# Revit family: RE-SERIES
name_source: partatom
category: Generic Models
revit_build: Autodesk Revit LT 2016 (Build: 20161004_0715(x64)
units: mm (PartAtom-declared; Revit-internal decimal feet)

## family parameters
Always vertical = Yes
Can host rebar = No
Cut with Voids When Loaded = No
Part Type = Normal
Room Calculation Point = No
Round Connector Dimension = Use Diameter
Shared = No
Work Plane-Based = No

## types (6) — shared parameters
Manufacturer = REVERSOMATIC
Submittals = http://www.reversomatic.com
URL = http://www.reversomatic.com

## per-type parameters (varying)
| type | A | B | BB | BBB | C | CC | D | DD | G | J | O | U | U2 |
| RE12 | 32.38 " | 24.62 " | 6.16 " | -6.16 " | 13.12 " | 6.56 " | 32 " | 27 " | 23.87 " | 6.5 " | 4.92 " | 154.54° | 52.39° |
| RE7 | 20.38 " | 16.62 " | 4.16 " | -4.16 " | 9 " | 4.5 " | 20 " | 15 " | 15.87 " | 2.5 " | 3.32 " | 140.00° | 60.00° |
| RE9 | 24.38 " | 19.38 " | 4.85 " | -4.85 " | 10.62 " | 5.31 " | 24 " | 19 " | 18.63 " | 9.47 " | 3.88 " | 146.74° | 60.19° |
| RE15 | 36.38 " | 28.38 " | 7.1 " | -7.1 " | 14.88 " | 7.44 " | 36 " | 31 " | 27.63 " | 8.5 " | 5.68 " | 146.74° | 60.19° |
| RE10 | 28.38 " | 21.38 " | 5.35 " | -5.35 " | 11.38 " | 5.69 " | 28 " | 23 " | 20.63 " | 7.06 " | 4.28 " | 146.74° | 60.19° |
| RE18 | 40.38 " | 33.75 " | 8.44 " | -8.44 " | 17.38 " | 8.69 " | 40 " | 35 " | 33 " | 8.5 " | 6.75 " | 146.74° | 60.19° |

note: column(s) folded — value = type name in every type: Model

## geometry (parser evidence)
native form markers: Sweep x3
no freeform markers — native parametric forms only
